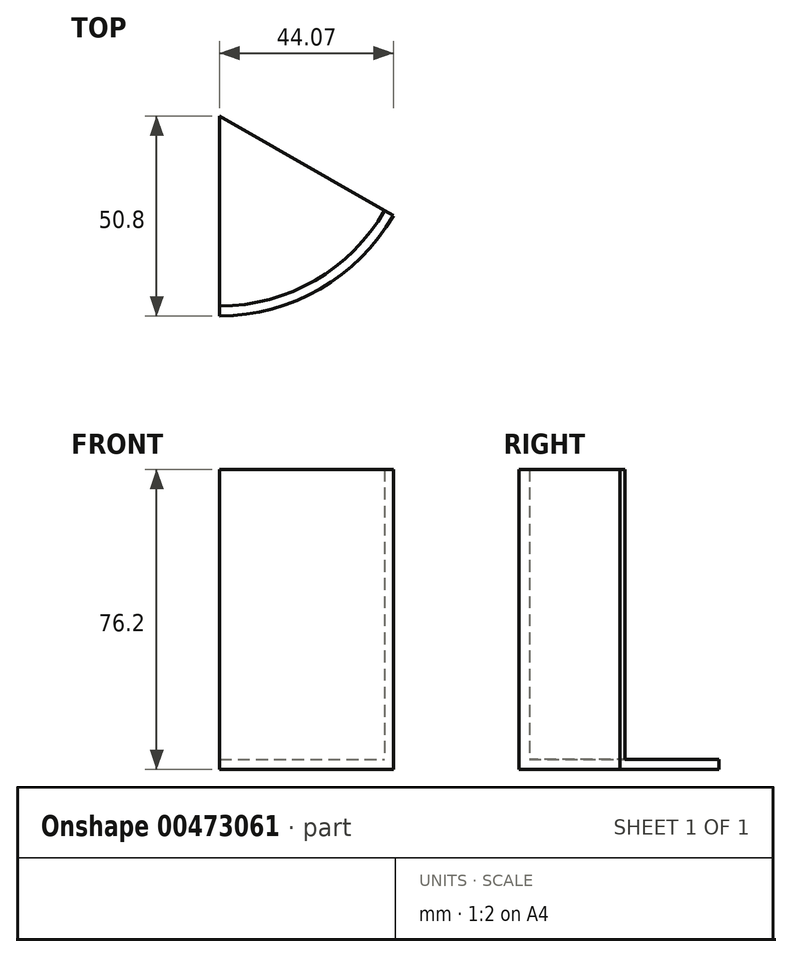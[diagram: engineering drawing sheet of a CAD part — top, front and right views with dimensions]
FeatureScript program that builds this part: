
annotation { "Feature Type Name" : "Feature", "Feature Type Description" : "" }
export const myFeature = defineFeature(function(context is Context, id is Id, definition is map)
    precondition{}
    {
        {
            var Q0;
            Q0=qCreatedBy(makeId("Top.planeOp"),FACE);
            var sketch = newSketch(context, id + "F0", { "sketchPlane" : qUnion([Q0])});
            skCircle(sketch, "E0", {"center": v(0, 0) * mm, "radius": 50.8 * mm});
            skSolve(sketch);
        }
        {
            var Q0;
            Q0 = qSketchRegion(id + "F0", true);
            extrude(context, id + "F1", {"entities" : qUnion([Q0]), "depth" : 76.2 * mm});
        }
        {
            var Q0;
            Q0=makeQuery(id+"F1.opExtrude","CAP_FACE",FACE,{"disambiguationData":[OSD([sQuery(id+"F0.wireOp",EDGE,"E0")])],"isStart":false});
            var sketch = newSketch(context, id + "F2", { "sketchPlane" : qUnion([Q0])});
            skLineSegment(sketch, "E1", {"start": v(0, 0) * mm, "end": v(0, -50.8) * mm});
            skLineSegment(sketch, "E2", {"start": v(0, 0) * mm, "end": v(44.07, -25.26) * mm});
            skSolve(sketch);
        }
        {
            var Q0;
            Q0=makeQuery(id+"F1.opExtrude","CAP_FACE",FACE,{"disambiguationData":[OSD([sQuery(id+"F0.wireOp",EDGE,"E0")])],"isStart":false});
            shell(context, id + "F3", {"entities" : qUnion([Q0]), "thickness" : 2.54 * mm});
        }
        {
            var Q0;
            {var subQ0=sQuery(id+"F2.wireOp",EDGE,"E1");Q0=makeQuery(id+"F2.imprint","IMPRINT",FACE,{"disambiguationData":[TD([[makeQuery(id+"F2.imprint","IMPRINT",EDGE,{"derivedFrom":subQ0}),-1.0]])]});}
            extrude(context, id + "F4", {"entities" : qUnion([Q0]), "operationType" : NewBodyOperationType.REMOVE, "oppositeDirection" : true, "depth" : 76.2 * mm});
        }
    });
